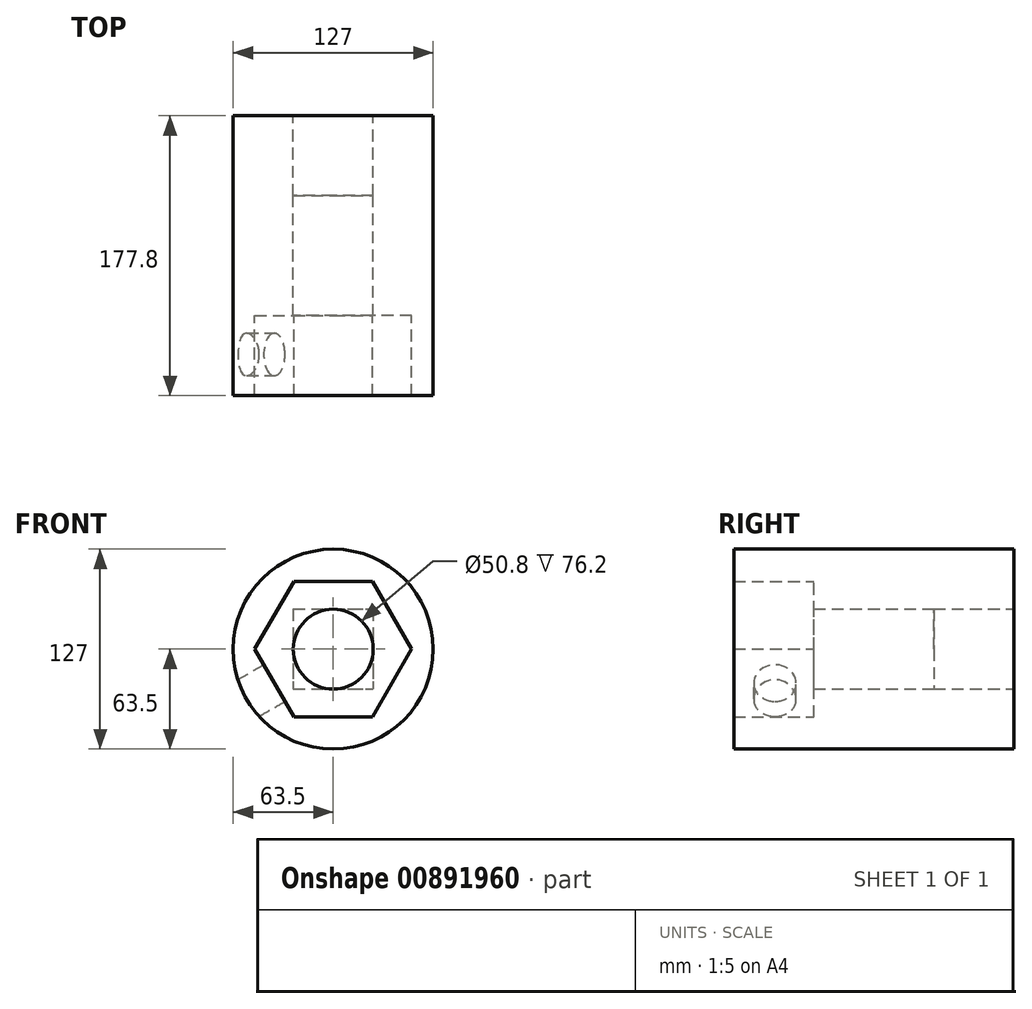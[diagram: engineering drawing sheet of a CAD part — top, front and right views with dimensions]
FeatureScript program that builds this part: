
annotation { "Feature Type Name" : "Feature", "Feature Type Description" : "" }
export const myFeature = defineFeature(function(context is Context, id is Id, definition is map)
    precondition{}
    {
        {
            var Q0;
            Q0=qCreatedBy(makeId("Front.planeOp"),FACE);
            var sketch = newSketch(context, id + "F0", { "sketchPlane" : qUnion([Q0])});
            skCircle(sketch, "E0", {"center": v(0, 0) * mm, "radius": 63.5 * mm});
            skSolve(sketch);
        }
        {
            var Q0;
            Q0=qSketchRegion(id+"F0",true);
            extrude(context, id + "F1", {"entities" : qUnion([Q0]), "depth" : 127 * mm});
        }
        {
            var Q0;
            Q0=qCreatedBy(makeId("Front.planeOp"),FACE);
            var sketch = newSketch(context, id + "F2", { "sketchPlane" : qUnion([Q0])});
            skLineSegment(sketch, "E1.bottom", {"start": v(-25.4, 25.4) * mm, "end": v(25.4, 25.4) * mm});
            skLineSegment(sketch, "E1.top", {"start": v(-25.4, -25.4) * mm, "end": v(25.4, -25.4) * mm});
            skLineSegment(sketch, "E1.left", {"start": v(-25.4, 25.4) * mm, "end": v(-25.4, -25.4) * mm});
            skLineSegment(sketch, "E1.right", {"start": v(25.4, 25.4) * mm, "end": v(25.4, -25.4) * mm});
            skPoint(sketch, "E1.middle", {"position": v(0, 0) * mm});
            skCircle(sketch, "E2", {"center": v(0, 0) * mm, "radius": 25.4 * mm});
            skSolve(sketch);
        }
        {
            var Q0;
            {var subQ0=sQuery(id+"F2.wireOp",EDGE,"E2");var subQ1=makeQuery(id+"F2.imprint","INTERSECT",VERTEX,{"derivedFrom":[sQuery(id+"F2.wireOp",EDGE,"E1.bottom"),subQ0]});Q0=makeQuery(id+"F2.imprint","IMPRINT",FACE,{"disambiguationData":[TD([[makeQuery(id+"F2.imprint","IMPRINT",EDGE,{"disambiguationData":[TD([[subQ1,1.0]])],"derivedFrom":subQ0}),1.0]])]});}
            var Q1;
            Q1=sQuery(id+"F2.wireOp",EDGE,"E2");
            extrude(context, id + "F3", {"entities" : qUnion([Q0]), "operationType" : NewBodyOperationType.REMOVE, "surfaceEntities" : qUnion([Q1]), "endBound" : BoundingType.THROUGH_ALL, "depth" : 25.4 * mm});
        }
        {
            var Q0;
            Q0=qSketchRegion(id+"F2",true);
            extrude(context, id + "F4", {"entities" : qUnion([Q0]), "operationType" : NewBodyOperationType.REMOVE, "depth" : 50.8 * mm});
        }
        {
            var Q0;
            Q0=makeQuery(id+"F1.opExtrude","CAP_FACE",FACE,{"disambiguationData":[OSD([sQuery(id+"F0.wireOp",EDGE,"E0")])],"isStart":false});
            var sketch = newSketch(context, id + "F5", { "sketchPlane" : qUnion([Q0])});
            skCircle(sketch, "E3.cCircle", {"center": v(0, 0) * mm, "radius": 43.16 * mm, "construction": true});
            skLineSegment(sketch, "E3.0", {"start": v(-24.92, 43.16) * mm, "end": v(24.92, 43.16) * mm});
            skLineSegment(sketch, "E3.1", {"start": v(24.92, 43.16) * mm, "end": v(49.84, 0) * mm});
            skLineSegment(sketch, "E3.2", {"start": v(49.84, 0) * mm, "end": v(24.92, -43.16) * mm});
            skLineSegment(sketch, "E3.3", {"start": v(24.92, -43.16) * mm, "end": v(-24.92, -43.16) * mm});
            skLineSegment(sketch, "E3.4", {"start": v(-24.92, -43.16) * mm, "end": v(-49.84, 0) * mm});
            skLineSegment(sketch, "E3.5", {"start": v(-49.84, 0) * mm, "end": v(-24.92, 43.16) * mm});
            skPoint(sketch, "E3.0.midPoint", {"position": v(0, 43.16) * mm});
            skSolve(sketch);
        }
        {
            var Q0;
            Q0=makeQuery(id+"F5.imprint","IMPRINT",FACE,{"disambiguationData":[TD([[makeQuery(id+"F5.imprint","IMPRINT",EDGE,{"derivedFrom":sQuery(id+"F5.wireOp",EDGE,"E3.0")}),1.0]])]});
            extrude(context, id + "F6", {"entities" : qUnion([Q0]), "operationType" : NewBodyOperationType.ADD, "depth" : 50.8 * mm});
        }
        {
            var Q0;
            Q0=makeQuery(id+"F6.opExtrude","SWEPT_FACE",FACE,{"disambiguationData":[OSD([sQuery(id+"F5.wireOp",EDGE,"E3.4")])]});
            var sketch = newSketch(context, id + "F7", { "sketchPlane" : qUnion([Q0])});
            skCircle(sketch, "E4", {"center": v(-151.62, 0) * mm, "radius": 13.48 * mm});
            skSolve(sketch);
        }
        {
            var Q0;
            Q0=makeQuery(id+"F7.imprint","IMPRINT",FACE,{"disambiguationData":[TD([[makeQuery(id+"F7.imprint","IMPRINT",EDGE,{"derivedFrom":sQuery(id+"F7.wireOp",EDGE,"E4")}),1.0]])]});
            extrude(context, id + "F8", {"entities" : qUnion([Q0]), "operationType" : NewBodyOperationType.REMOVE, "endBound" : BoundingType.THROUGH_ALL, "oppositeDirection" : true, "depth" : 25.4 * mm, "offsetDistance" : 25.4 * mm});
        }
    });
